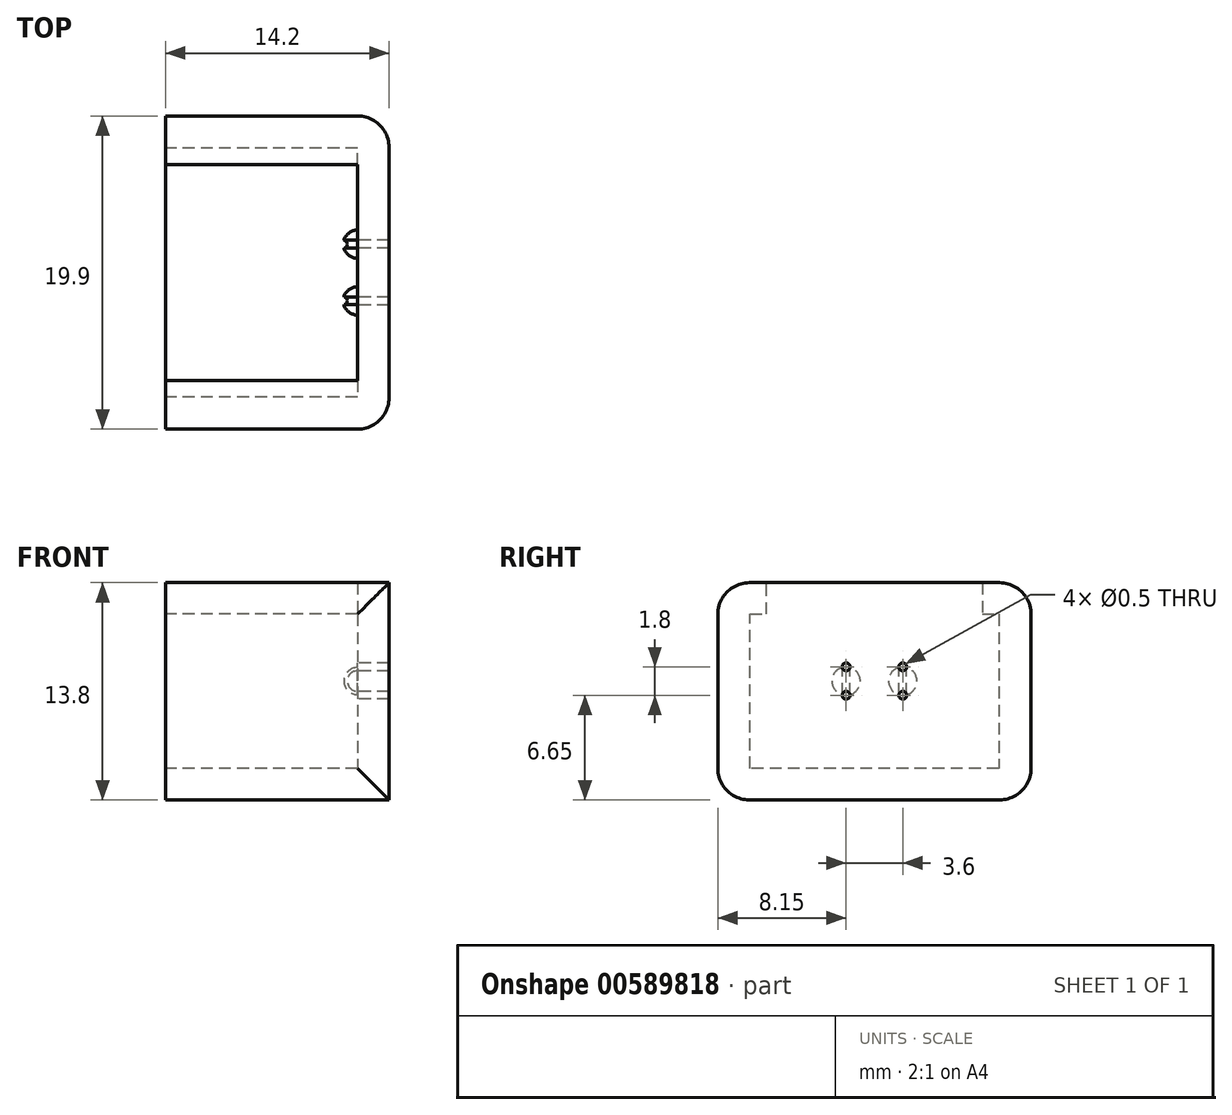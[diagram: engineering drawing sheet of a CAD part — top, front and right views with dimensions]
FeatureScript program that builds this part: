
annotation { "Feature Type Name" : "Feature", "Feature Type Description" : "" }
export const myFeature = defineFeature(function(context is Context, id is Id, definition is map)
    precondition{}
    {
        {
            var Q0;
            Q0=qCreatedBy(makeId("Top.planeOp"),FACE);
            var sketch = newSketch(context, id + "F0", { "sketchPlane" : qUnion([Q0])});
            skLineSegment(sketch, "E0.bottom", {"start": v(0, 0) * mm, "end": v(14.2, 0) * mm});
            skLineSegment(sketch, "E0.top", {"start": v(0, 19.9) * mm, "end": v(14.2, 19.9) * mm});
            skLineSegment(sketch, "E0.left", {"start": v(0, 0) * mm, "end": v(0, 19.9) * mm});
            skLineSegment(sketch, "E0.right", {"start": v(14.2, 0) * mm, "end": v(14.2, 19.9) * mm});
            skSolve(sketch);
        }
        {
            var Q0;
            {var subQ1=sQuery(id+"F0.wireOp",EDGE,"E0.bottom");Q0=makeQuery(id+"F0.imprint","IMPRINT",FACE,{"disambiguationData":[TD([[makeQuery(id+"F0.imprint","IMPRINT",EDGE,{"derivedFrom":subQ1}),1.0]])]});}
            extrude(context, id + "F1", {"entities" : qUnion([Q0]), "depth" : 13.8 * mm, "offsetDistance" : 25 * mm});
        }
        {
            var Q0;
            Q0 = qSketchRegion(id + "F0", true);
            extrude(context, id + "F2", {"entities" : qUnion([Q0]), "operationType" : NewBodyOperationType.ADD, "depth" : 12 * mm, "offsetDistance" : 25 * mm});
        }
        {
            var Q0;
            Q0=makeQuery(id+"F1.opExtrude","SWEPT_FACE",FACE,{"disambiguationData":[OSD([sQuery(id+"F0.wireOp",EDGE,"E0.left")])]});
            var sketch = newSketch(context, id + "F3", { "sketchPlane" : qUnion([Q0])});
            skLineSegment(sketch, "E1", {"start": v(-16.8, 13.8) * mm, "end": v(-16.8, 11.8) * mm});
            skLineSegment(sketch, "E2", {"start": v(-16.8, 11.8) * mm, "end": v(-17.85, 11.8) * mm});
            skLineSegment(sketch, "E3", {"start": v(-17.85, 11.8) * mm, "end": v(-17.85, 2) * mm});
            skLineSegment(sketch, "E4", {"start": v(-17.85, 2) * mm, "end": v(-2.05, 2) * mm});
            skLineSegment(sketch, "E5", {"start": v(-2.05, 2) * mm, "end": v(-2.05, 11.8) * mm});
            skLineSegment(sketch, "E6", {"start": v(-2.05, 11.8) * mm, "end": v(-3.1, 11.8) * mm});
            skLineSegment(sketch, "E7", {"start": v(-3.1, 11.8) * mm, "end": v(-3.1, 13.8) * mm});
            skLineSegment(sketch, "E8", {"start": v(-9.95, 0) * mm, "end": v(-9.95, 13.8) * mm, "construction": true});
            skLineSegment(sketch, "E9", {"start": v(-19.9, 6.9) * mm, "end": v(0, 6.9) * mm, "construction": true});
            skLineSegment(sketch, "E10", {"start": v(-16.8, 13.8) * mm, "end": v(-3.1, 13.8) * mm});
            skSolve(sketch);
        }
        {
            var Q0;
            Q0 = qSketchRegion(id + "F3", true);
            extrude(context, id + "F4", {"entities" : qUnion([Q0]), "operationType" : NewBodyOperationType.REMOVE, "oppositeDirection" : true, "depth" : 12.2 * mm, "offsetDistance" : 25 * mm});
        }
        {
            var Q0;
            Q0=makeQuery(id+"F4.boolean.opBoolean","COPY",FACE,{"derivedFrom":makeQuery(id+"F4.opExtrude","CAP_FACE",FACE,{"disambiguationData":[OSD([sQuery(id+"F3.wireOp",EDGE,"E1"),sQuery(id+"F3.wireOp",EDGE,"E2"),sQuery(id+"F3.wireOp",EDGE,"E3"),sQuery(id+"F3.wireOp",EDGE,"E4"),sQuery(id+"F3.wireOp",EDGE,"E5"),sQuery(id+"F3.wireOp",EDGE,"E6"),sQuery(id+"F3.wireOp",EDGE,"E7"),sQuery(id+"F3.wireOp",EDGE,"E10")])],"isStart":false})});
            var sketch = newSketch(context, id + "F5", { "sketchPlane" : qUnion([Q0])});
            skLineSegment(sketch, "E11", {"start": v(-9.95, 13.8) * mm, "end": v(-9.95, 2) * mm, "construction": true});
            skLineSegment(sketch, "E12.bottom", {"start": v(-12.95, 6.05) * mm, "end": v(-6.95, 6.05) * mm});
            skLineSegment(sketch, "E12.top", {"start": v(-12.95, 9.05) * mm, "end": v(-6.95, 9.05) * mm});
            skLineSegment(sketch, "E12.left", {"start": v(-12.95, 6.05) * mm, "end": v(-12.95, 9.05) * mm});
            skLineSegment(sketch, "E12.right", {"start": v(-6.95, 6.05) * mm, "end": v(-6.95, 9.05) * mm});
            skCircle(sketch, "E13", {"center": v(-11.75, 7.55) * mm, "radius": 0.9 * mm});
            skCircle(sketch, "E14", {"center": v(-8.15, 7.55) * mm, "radius": 0.9 * mm});
            skCircle(sketch, "E15", {"center": v(-8.15, 8.45) * mm, "radius": 0.25 * mm});
            skCircle(sketch, "E16", {"center": v(-8.15, 6.65) * mm, "radius": 0.25 * mm});
            skCircle(sketch, "E17", {"center": v(-11.75, 6.65) * mm, "radius": 0.25 * mm});
            skCircle(sketch, "E18", {"center": v(-11.75, 8.45) * mm, "radius": 0.25 * mm});
            skLineSegment(sketch, "E19", {"start": v(-12.65, 7.55) * mm, "end": v(-10.85, 7.55) * mm});
            skLineSegment(sketch, "E20", {"start": v(-9.05, 7.55) * mm, "end": v(-7.25, 7.55) * mm});
            skSolve(sketch);
        }
        {
            var Q0;
            Q0=makeQuery(id+"F5.imprint","IMPRINT",FACE,{"disambiguationData":[TD([[makeQuery(id+"F5.imprint","IMPRINT",EDGE,{"derivedFrom":sQuery(id+"F5.wireOp",EDGE,"E18")}),1.0]])]});
            var Q1;
            Q1=makeQuery(id+"F5.imprint","IMPRINT",FACE,{"disambiguationData":[TD([[makeQuery(id+"F5.imprint","IMPRINT",EDGE,{"derivedFrom":sQuery(id+"F5.wireOp",EDGE,"E15")}),1.0]])]});
            var Q2;
            Q2=makeQuery(id+"F5.imprint","IMPRINT",FACE,{"disambiguationData":[TD([[makeQuery(id+"F5.imprint","IMPRINT",EDGE,{"derivedFrom":sQuery(id+"F5.wireOp",EDGE,"E16")}),1.0]])]});
            var Q3;
            Q3=makeQuery(id+"F5.imprint","IMPRINT",FACE,{"disambiguationData":[TD([[makeQuery(id+"F5.imprint","IMPRINT",EDGE,{"derivedFrom":sQuery(id+"F5.wireOp",EDGE,"E17")}),1.0]])]});
            extrude(context, id + "F6", {"entities" : qUnion([Q0, Q1, Q2, Q3]), "operationType" : NewBodyOperationType.REMOVE, "endBound" : BoundingType.THROUGH_ALL, "oppositeDirection" : true, "depth" : 25 * mm, "offsetDistance" : 25 * mm});
        }
        {
            var Q0;
            {var subQ0=sQuery(id+"F5.wireOp",EDGE,"E19");Q0=makeQuery(id+"F5.imprint","IMPRINT",FACE,{"disambiguationData":[TD([[makeQuery(id+"F5.imprint","IMPRINT",EDGE,{"derivedFrom":subQ0}),1.0]])]});}
            var Q1;
            {var subQ0=sQuery(id+"F5.wireOp",EDGE,"E20");Q1=makeQuery(id+"F5.imprint","IMPRINT",FACE,{"disambiguationData":[TD([[makeQuery(id+"F5.imprint","IMPRINT",EDGE,{"derivedFrom":subQ0}),1.0]])]});}
            var Q2;
            Q2=sQuery(id+"F5.wireOp",EDGE,"E19");
            revolve(context, id + "F7", {"operationType" : NewBodyOperationType.ADD, "entities" : qUnion([Q0, Q1]), "axis" : qUnion([Q2]), "revolveType" : RevolveType.ONE_DIRECTION, "angle" : 180 * degree});
        }
        {
            var Q0;
            Q0=makeQuery(id+"F1.opExtrude","CAP_EDGE",EDGE,{"disambiguationData":[OSD([sQuery(id+"F0.wireOp",EDGE,"E0.bottom")])],"isStart":true});
            var Q1;
            Q1=makeQuery(id+"F1.opExtrude","CAP_EDGE",EDGE,{"disambiguationData":[OSD([sQuery(id+"F0.wireOp",EDGE,"E0.top")])],"isStart":true});
            var Q2;
            Q2=makeQuery(id+"F1.opExtrude","CAP_EDGE",EDGE,{"disambiguationData":[OSD([sQuery(id+"F0.wireOp",EDGE,"E0.top")])],"isStart":false});
            var Q3;
            Q3=makeQuery(id+"F1.opExtrude","CAP_EDGE",EDGE,{"disambiguationData":[OSD([sQuery(id+"F0.wireOp",EDGE,"E0.bottom")])],"isStart":false});
            var Q4;
            Q4=makeQuery(id+"F1.opExtrude","SWEPT_EDGE",EDGE,{"disambiguationData":[OSD([sQuery(id+"F0.wireOp",EDGE,"E0.bottom"),sQuery(id+"F0.wireOp",EDGE,"E0.right")])]});
            var Q5;
            Q5=makeQuery(id+"F1.opExtrude","SWEPT_EDGE",EDGE,{"disambiguationData":[OSD([sQuery(id+"F0.wireOp",EDGE,"E0.top"),sQuery(id+"F0.wireOp",EDGE,"E0.right")])]});
            fillet(context, id + "F8", {"entities" : qUnion([Q0, Q1, Q2, Q3, Q4, Q5]), "radius" : 2 * mm, "tangentPropagation" : true, "allowEdgeOverflow" : false});
        }
    });
